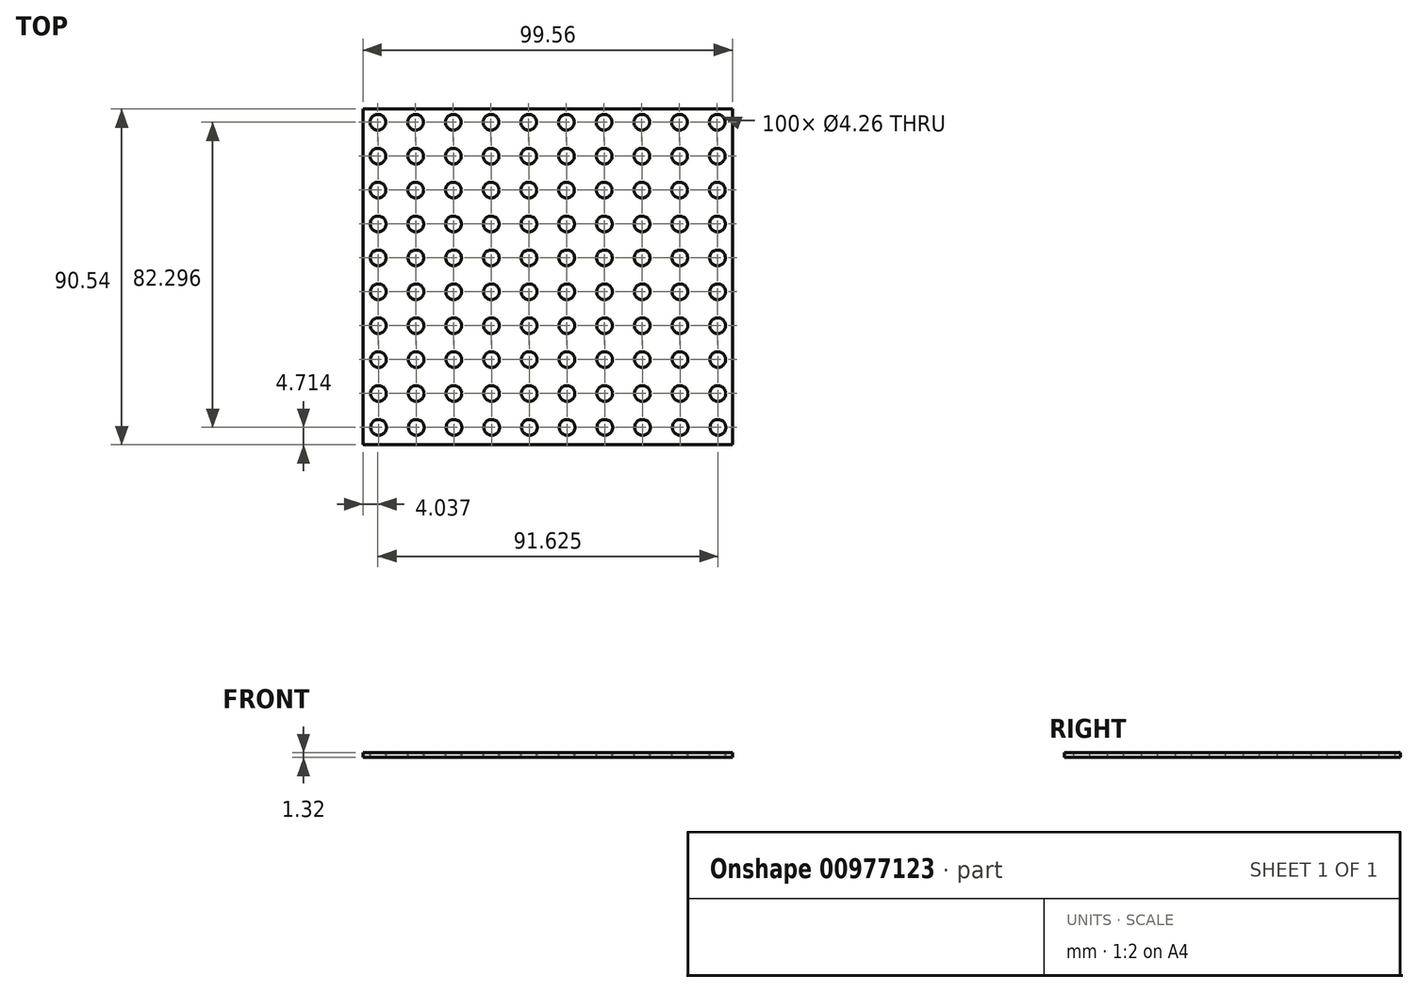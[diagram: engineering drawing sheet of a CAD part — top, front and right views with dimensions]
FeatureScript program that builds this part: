
annotation { "Feature Type Name" : "Feature", "Feature Type Description" : "" }
export const myFeature = defineFeature(function(context is Context, id is Id, definition is map)
    precondition{}
    {
        {
            var Q0;
            Q0=qCreatedBy(makeId("Top.planeOp"),FACE);
            var sketch = newSketch(context, id + "F0", { "sketchPlane" : qUnion([Q0])});
            skLineSegment(sketch, "E0.bottom", {"start": v(49.78, -45.27) * mm, "end": v(-49.78, -45.27) * mm});
            skLineSegment(sketch, "E0.top", {"start": v(49.78, 45.27) * mm, "end": v(-49.78, 45.27) * mm});
            skLineSegment(sketch, "E0.left", {"start": v(49.78, -45.27) * mm, "end": v(49.78, 45.27) * mm});
            skLineSegment(sketch, "E0.right", {"start": v(-49.78, -45.27) * mm, "end": v(-49.78, 45.27) * mm});
            skPoint(sketch, "E0.middle", {"position": v(0, 0) * mm});
            skSolve(sketch);
        }
        {
            var Q0;
            Q0 = qSketchRegion(id + "F0", true);
            extrude(context, id + "F1", {"entities" : qUnion([Q0]), "depth" : 1.32 * mm, "offsetDistance" : 25.4 * mm});
        }
        {
            var Q0;
            Q0=makeQuery(id+"F1.opExtrude","CAP_FACE",FACE,{"disambiguationData":[OSD([sQuery(id+"F0.wireOp",EDGE,"E0.bottom"),sQuery(id+"F0.wireOp",EDGE,"E0.top"),sQuery(id+"F0.wireOp",EDGE,"E0.left"),sQuery(id+"F0.wireOp",EDGE,"E0.right")])],"isStart":false});
            var sketch = newSketch(context, id + "F2", { "sketchPlane" : qUnion([Q0])});
            skCircle(sketch, "E1", {"center": v(-45.74, 41.74) * mm, "radius": 2.13 * mm});
            skCircle(sketch, "E2.1.0.0", {"center": v(-35.58, 41.74) * mm, "radius": 2.13 * mm});
            skCircle(sketch, "E2.2.0.0", {"center": v(-25.42, 41.74) * mm, "radius": 2.13 * mm});
            skCircle(sketch, "E2.3.0.0", {"center": v(-15.26, 41.74) * mm, "radius": 2.13 * mm});
            skCircle(sketch, "E2.4.0.0", {"center": v(-5.1, 41.74) * mm, "radius": 2.13 * mm});
            skCircle(sketch, "E2.5.0.0", {"center": v(5.06, 41.74) * mm, "radius": 2.13 * mm});
            skCircle(sketch, "E2.6.0.0", {"center": v(15.22, 41.74) * mm, "radius": 2.13 * mm});
            skCircle(sketch, "E2.7.0.0", {"center": v(25.38, 41.74) * mm, "radius": 2.13 * mm});
            skCircle(sketch, "E2.8.0.0", {"center": v(35.54, 41.74) * mm, "radius": 2.13 * mm});
            skCircle(sketch, "E2.9.0.0", {"center": v(45.7, 41.74) * mm, "radius": 2.13 * mm});
            skCircle(sketch, "E3.1.0.0", {"center": v(-45.72, 32.6) * mm, "radius": 2.13 * mm});
            skCircle(sketch, "E3.1.0.1", {"center": v(-25.4, 32.6) * mm, "radius": 2.13 * mm});
            skCircle(sketch, "E3.1.0.2", {"center": v(45.72, 32.6) * mm, "radius": 2.13 * mm});
            skCircle(sketch, "E3.1.0.3", {"center": v(15.24, 32.6) * mm, "radius": 2.13 * mm});
            skCircle(sketch, "E3.1.0.4", {"center": v(-5.08, 32.6) * mm, "radius": 2.13 * mm});
            skCircle(sketch, "E3.1.0.5", {"center": v(35.56, 32.6) * mm, "radius": 2.13 * mm});
            skCircle(sketch, "E3.1.0.6", {"center": v(-15.24, 32.6) * mm, "radius": 2.13 * mm});
            skCircle(sketch, "E3.1.0.7", {"center": v(5.08, 32.6) * mm, "radius": 2.13 * mm});
            skCircle(sketch, "E3.1.0.8", {"center": v(25.4, 32.6) * mm, "radius": 2.13 * mm});
            skCircle(sketch, "E3.1.0.9", {"center": v(-35.56, 32.6) * mm, "radius": 2.13 * mm});
            skCircle(sketch, "E3.2.0.0", {"center": v(-45.7, 23.45) * mm, "radius": 2.13 * mm});
            skCircle(sketch, "E3.2.0.1", {"center": v(-25.38, 23.45) * mm, "radius": 2.13 * mm});
            skCircle(sketch, "E3.2.0.2", {"center": v(45.74, 23.45) * mm, "radius": 2.13 * mm});
            skCircle(sketch, "E3.2.0.3", {"center": v(15.26, 23.45) * mm, "radius": 2.13 * mm});
            skCircle(sketch, "E3.2.0.4", {"center": v(-5.06, 23.45) * mm, "radius": 2.13 * mm});
            skCircle(sketch, "E3.2.0.5", {"center": v(35.58, 23.45) * mm, "radius": 2.13 * mm});
            skCircle(sketch, "E3.2.0.6", {"center": v(-15.22, 23.45) * mm, "radius": 2.13 * mm});
            skCircle(sketch, "E3.2.0.7", {"center": v(5.1, 23.45) * mm, "radius": 2.13 * mm});
            skCircle(sketch, "E3.2.0.8", {"center": v(25.42, 23.45) * mm, "radius": 2.13 * mm});
            skCircle(sketch, "E3.2.0.9", {"center": v(-35.54, 23.45) * mm, "radius": 2.13 * mm});
            skCircle(sketch, "E3.3.0.0", {"center": v(-45.68, 14.3) * mm, "radius": 2.13 * mm});
            skCircle(sketch, "E3.3.0.1", {"center": v(-25.36, 14.3) * mm, "radius": 2.13 * mm});
            skCircle(sketch, "E3.3.0.2", {"center": v(45.76, 14.3) * mm, "radius": 2.13 * mm});
            skCircle(sketch, "E3.3.0.3", {"center": v(15.28, 14.3) * mm, "radius": 2.13 * mm});
            skCircle(sketch, "E3.3.0.4", {"center": v(-5.04, 14.3) * mm, "radius": 2.13 * mm});
            skCircle(sketch, "E3.3.0.5", {"center": v(35.6, 14.3) * mm, "radius": 2.13 * mm});
            skCircle(sketch, "E3.3.0.6", {"center": v(-15.2, 14.3) * mm, "radius": 2.13 * mm});
            skCircle(sketch, "E3.3.0.7", {"center": v(5.12, 14.3) * mm, "radius": 2.13 * mm});
            skCircle(sketch, "E3.3.0.8", {"center": v(25.44, 14.3) * mm, "radius": 2.13 * mm});
            skCircle(sketch, "E3.3.0.9", {"center": v(-35.52, 14.3) * mm, "radius": 2.13 * mm});
            skCircle(sketch, "E3.4.0.0", {"center": v(-45.66, 5.16) * mm, "radius": 2.13 * mm});
            skCircle(sketch, "E3.4.0.1", {"center": v(-25.34, 5.16) * mm, "radius": 2.13 * mm});
            skCircle(sketch, "E3.4.0.2", {"center": v(45.78, 5.16) * mm, "radius": 2.13 * mm});
            skCircle(sketch, "E3.4.0.3", {"center": v(15.3, 5.16) * mm, "radius": 2.13 * mm});
            skCircle(sketch, "E3.4.0.4", {"center": v(-5.02, 5.16) * mm, "radius": 2.13 * mm});
            skCircle(sketch, "E3.4.0.5", {"center": v(35.62, 5.16) * mm, "radius": 2.13 * mm});
            skCircle(sketch, "E3.4.0.6", {"center": v(-15.18, 5.16) * mm, "radius": 2.13 * mm});
            skCircle(sketch, "E3.4.0.7", {"center": v(5.14, 5.16) * mm, "radius": 2.13 * mm});
            skCircle(sketch, "E3.4.0.8", {"center": v(25.46, 5.16) * mm, "radius": 2.13 * mm});
            skCircle(sketch, "E3.4.0.9", {"center": v(-35.5, 5.16) * mm, "radius": 2.13 * mm});
            skCircle(sketch, "E3.5.0.0", {"center": v(-45.64, -3.98) * mm, "radius": 2.13 * mm});
            skCircle(sketch, "E3.5.0.1", {"center": v(-25.32, -3.98) * mm, "radius": 2.13 * mm});
            skCircle(sketch, "E3.5.0.2", {"center": v(45.8, -3.98) * mm, "radius": 2.13 * mm});
            skCircle(sketch, "E3.5.0.3", {"center": v(15.32, -3.98) * mm, "radius": 2.13 * mm});
            skCircle(sketch, "E3.5.0.4", {"center": v(-5, -3.98) * mm, "radius": 2.13 * mm});
            skCircle(sketch, "E3.5.0.5", {"center": v(35.64, -3.98) * mm, "radius": 2.13 * mm});
            skCircle(sketch, "E3.5.0.6", {"center": v(-15.16, -3.98) * mm, "radius": 2.13 * mm});
            skCircle(sketch, "E3.5.0.7", {"center": v(5.16, -3.98) * mm, "radius": 2.13 * mm});
            skCircle(sketch, "E3.5.0.8", {"center": v(25.48, -3.98) * mm, "radius": 2.13 * mm});
            skCircle(sketch, "E3.5.0.9", {"center": v(-35.48, -3.98) * mm, "radius": 2.13 * mm});
            skCircle(sketch, "E3.6.0.0", {"center": v(-45.62, -13.12) * mm, "radius": 2.13 * mm});
            skCircle(sketch, "E3.6.0.1", {"center": v(-25.3, -13.12) * mm, "radius": 2.13 * mm});
            skCircle(sketch, "E3.6.0.2", {"center": v(45.82, -13.12) * mm, "radius": 2.13 * mm});
            skCircle(sketch, "E3.6.0.3", {"center": v(15.34, -13.12) * mm, "radius": 2.13 * mm});
            skCircle(sketch, "E3.6.0.4", {"center": v(-4.98, -13.12) * mm, "radius": 2.13 * mm});
            skCircle(sketch, "E3.6.0.5", {"center": v(35.66, -13.12) * mm, "radius": 2.13 * mm});
            skCircle(sketch, "E3.6.0.6", {"center": v(-15.14, -13.12) * mm, "radius": 2.13 * mm});
            skCircle(sketch, "E3.6.0.7", {"center": v(5.18, -13.12) * mm, "radius": 2.13 * mm});
            skCircle(sketch, "E3.6.0.8", {"center": v(25.5, -13.12) * mm, "radius": 2.13 * mm});
            skCircle(sketch, "E3.6.0.9", {"center": v(-35.46, -13.12) * mm, "radius": 2.13 * mm});
            skCircle(sketch, "E3.7.0.0", {"center": v(-45.6, -22.27) * mm, "radius": 2.13 * mm});
            skCircle(sketch, "E3.7.0.1", {"center": v(-25.28, -22.27) * mm, "radius": 2.13 * mm});
            skCircle(sketch, "E3.7.0.2", {"center": v(45.84, -22.27) * mm, "radius": 2.13 * mm});
            skCircle(sketch, "E3.7.0.3", {"center": v(15.36, -22.27) * mm, "radius": 2.13 * mm});
            skCircle(sketch, "E3.7.0.4", {"center": v(-4.96, -22.27) * mm, "radius": 2.13 * mm});
            skCircle(sketch, "E3.7.0.5", {"center": v(35.68, -22.27) * mm, "radius": 2.13 * mm});
            skCircle(sketch, "E3.7.0.6", {"center": v(-15.12, -22.27) * mm, "radius": 2.13 * mm});
            skCircle(sketch, "E3.7.0.7", {"center": v(5.2, -22.27) * mm, "radius": 2.13 * mm});
            skCircle(sketch, "E3.7.0.8", {"center": v(25.52, -22.27) * mm, "radius": 2.13 * mm});
            skCircle(sketch, "E3.7.0.9", {"center": v(-35.44, -22.27) * mm, "radius": 2.13 * mm});
            skCircle(sketch, "E3.8.0.0", {"center": v(-45.58, -31.41) * mm, "radius": 2.13 * mm});
            skCircle(sketch, "E3.8.0.1", {"center": v(-25.26, -31.41) * mm, "radius": 2.13 * mm});
            skCircle(sketch, "E3.8.0.2", {"center": v(45.86, -31.41) * mm, "radius": 2.13 * mm});
            skCircle(sketch, "E3.8.0.3", {"center": v(15.38, -31.41) * mm, "radius": 2.13 * mm});
            skCircle(sketch, "E3.8.0.4", {"center": v(-4.94, -31.41) * mm, "radius": 2.13 * mm});
            skCircle(sketch, "E3.8.0.5", {"center": v(35.7, -31.41) * mm, "radius": 2.13 * mm});
            skCircle(sketch, "E3.8.0.6", {"center": v(-15.1, -31.41) * mm, "radius": 2.13 * mm});
            skCircle(sketch, "E3.8.0.7", {"center": v(5.22, -31.41) * mm, "radius": 2.13 * mm});
            skCircle(sketch, "E3.8.0.8", {"center": v(25.54, -31.41) * mm, "radius": 2.13 * mm});
            skCircle(sketch, "E3.8.0.9", {"center": v(-35.42, -31.41) * mm, "radius": 2.13 * mm});
            skCircle(sketch, "E3.9.0.0", {"center": v(-45.56, -40.56) * mm, "radius": 2.13 * mm});
            skCircle(sketch, "E3.9.0.1", {"center": v(-25.24, -40.56) * mm, "radius": 2.13 * mm});
            skCircle(sketch, "E3.9.0.2", {"center": v(45.88, -40.56) * mm, "radius": 2.13 * mm});
            skCircle(sketch, "E3.9.0.3", {"center": v(15.4, -40.56) * mm, "radius": 2.13 * mm});
            skCircle(sketch, "E3.9.0.4", {"center": v(-4.92, -40.56) * mm, "radius": 2.13 * mm});
            skCircle(sketch, "E3.9.0.5", {"center": v(35.72, -40.56) * mm, "radius": 2.13 * mm});
            skCircle(sketch, "E3.9.0.6", {"center": v(-15.08, -40.56) * mm, "radius": 2.13 * mm});
            skCircle(sketch, "E3.9.0.7", {"center": v(5.24, -40.56) * mm, "radius": 2.13 * mm});
            skCircle(sketch, "E3.9.0.8", {"center": v(25.56, -40.56) * mm, "radius": 2.13 * mm});
            skCircle(sketch, "E3.9.0.9", {"center": v(-35.4, -40.56) * mm, "radius": 2.13 * mm});
            skSolve(sketch);
        }
        {
            var Q0;
            Q0 = qSketchRegion(id + "F2", true);
            extrude(context, id + "F3", {"entities" : qUnion([Q0]), "operationType" : NewBodyOperationType.REMOVE, "oppositeDirection" : true, "depth" : 25.4 * mm, "offsetDistance" : 25.4 * mm});
        }
    });
